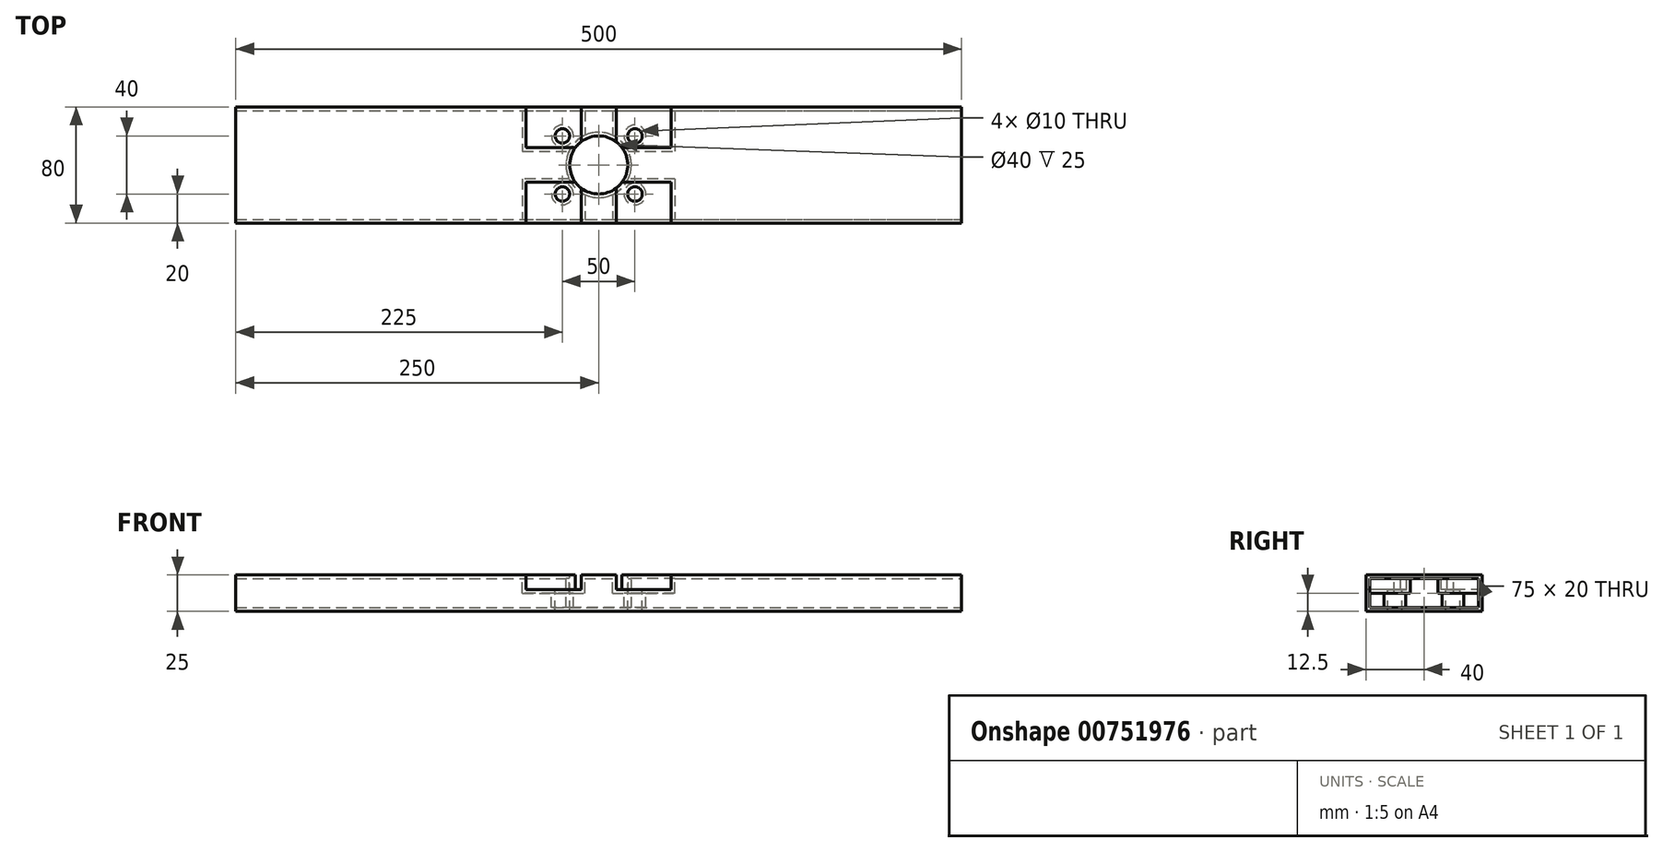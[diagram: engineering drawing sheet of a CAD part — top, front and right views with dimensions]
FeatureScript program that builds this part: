
annotation { "Feature Type Name" : "Feature", "Feature Type Description" : "" }
export const myFeature = defineFeature(function(context is Context, id is Id, definition is map)
    precondition{}
    {
        {
            var Q0;
            Q0=qCreatedBy(makeId("Top.planeOp"),FACE);
            var sketch = newSketch(context, id + "F0", { "sketchPlane" : qUnion([Q0])});
            skLineSegment(sketch, "E0.bottom", {"start": v(-250, 40) * mm, "end": v(250, 40) * mm});
            skLineSegment(sketch, "E0.top", {"start": v(-250, -40) * mm, "end": v(250, -40) * mm});
            skLineSegment(sketch, "E0.left", {"start": v(-250, 40) * mm, "end": v(-250, -40) * mm});
            skLineSegment(sketch, "E0.right", {"start": v(250, 40) * mm, "end": v(250, -40) * mm});
            skPoint(sketch, "E0.middle", {"position": v(0, 0) * mm});
            skSolve(sketch);
        }
        {
            var Q0;
            Q0=makeQuery(id+"F0.imprint","IMPRINT",FACE,{"disambiguationData":[TD([[makeQuery(id+"F0.imprint","IMPRINT",EDGE,{"derivedFrom":sQuery(id+"F0.wireOp",EDGE,"E0.bottom")}),-1.0]])]});
            extrude(context, id + "F1", {"entities" : qUnion([Q0]), "depth" : 25 * mm, "offsetDistance" : 25 * mm});
        }
        {
            var Q0;
            Q0=makeQuery(id+"F1.opExtrude","CAP_FACE",FACE,{"disambiguationData":[OSD([sQuery(id+"F0.wireOp",EDGE,"E0.bottom"),sQuery(id+"F0.wireOp",EDGE,"E0.top"),sQuery(id+"F0.wireOp",EDGE,"E0.left"),sQuery(id+"F0.wireOp",EDGE,"E0.right")])],"isStart":false});
            var sketch = newSketch(context, id + "F2", { "sketchPlane" : qUnion([Q0])});
            skLineSegment(sketch, "E1", {"start": v(0, 40) * mm, "end": v(0, -40) * mm, "construction": true});
            skLineSegment(sketch, "E2", {"start": v(-50, 40) * mm, "end": v(-50, -40) * mm});
            skLineSegment(sketch, "E3", {"start": v(50, 40) * mm, "end": v(50, -40) * mm});
            skLineSegment(sketch, "E4", {"start": v(-50, 0) * mm, "end": v(0, 0) * mm, "construction": true});
            skLineSegment(sketch, "E5", {"start": v(0, 0) * mm, "end": v(50, 0) * mm, "construction": true});
            skLineSegment(sketch, "E6", {"start": v(-25, 0) * mm, "end": v(-25, 40) * mm, "construction": true});
            skLineSegment(sketch, "E7", {"start": v(-25, 0) * mm, "end": v(-25, -40) * mm, "construction": true});
            skLineSegment(sketch, "E8", {"start": v(25, 0) * mm, "end": v(25, 40) * mm, "construction": true});
            skLineSegment(sketch, "E9", {"start": v(25, 0) * mm, "end": v(25, -40) * mm, "construction": true});
            skPoint(sketch, "E10", {"position": v(-25, 20) * mm});
            skPoint(sketch, "E11", {"position": v(25, 20) * mm});
            skPoint(sketch, "E12", {"position": v(25, -20) * mm});
            skPoint(sketch, "E13", {"position": v(-25, -20) * mm});
            skLineSegment(sketch, "E14", {"start": v(-12, 40) * mm, "end": v(-12, -40) * mm});
            skLineSegment(sketch, "E15", {"start": v(12, 40) * mm, "end": v(12, -40) * mm});
            skLineSegment(sketch, "E16", {"start": v(-50, 12) * mm, "end": v(50, 12) * mm});
            skLineSegment(sketch, "E17", {"start": v(50, -12) * mm, "end": v(-50, -12) * mm});
            skSolve(sketch);
        }
        {
            var Q0;
            Q0=sQuery(id+"F2.wireOp",VERTEX,"E5.start");
            var Q1;
            Q1=makeQuery(id+"F1.opExtrude","SWEPT_BODY",BODY,{"disambiguationData":[OSD([sQuery(id+"F0.wireOp",EDGE,"E0.bottom"),sQuery(id+"F0.wireOp",EDGE,"E0.top"),sQuery(id+"F0.wireOp",EDGE,"E0.left"),sQuery(id+"F0.wireOp",EDGE,"E0.right")])]});
            hole(context, id + "F3", {"style" : HoleStyle.SIMPLE, "endStyle" : HoleEndStyle.BLIND, "holeDiameter" : 40 * mm, "majorDiameter" : 5 * mm, "holeDepth" : 25 * mm, "isTappedThrough" : true, "tappedDepth" : 12 * mm, "tapClearance" : 3, "startFromSketch" : true, "locations" : qUnion([Q0]), "scope" : qUnion([Q1])});
        }
        {
            var Q0;
            Q0=sQuery(id+"F2.wireOp",VERTEX,"E10");
            var Q1;
            Q1=sQuery(id+"F2.wireOp",VERTEX,"E11");
            var Q2;
            Q2=sQuery(id+"F2.wireOp",VERTEX,"E12");
            var Q3;
            Q3=sQuery(id+"F2.wireOp",VERTEX,"E13");
            var Q4;
            Q4=makeQuery(id+"F1.opExtrude","SWEPT_BODY",BODY,{"disambiguationData":[OSD([sQuery(id+"F0.wireOp",EDGE,"E0.bottom"),sQuery(id+"F0.wireOp",EDGE,"E0.top"),sQuery(id+"F0.wireOp",EDGE,"E0.left"),sQuery(id+"F0.wireOp",EDGE,"E0.right")])]});
            hole(context, id + "F4", {"style" : HoleStyle.SIMPLE, "endStyle" : HoleEndStyle.BLIND, "holeDiameter" : 10 * mm, "majorDiameter" : 5 * mm, "holeDepth" : 25 * mm, "isTappedThrough" : true, "tappedDepth" : 12 * mm, "tapClearance" : 3, "startFromSketch" : true, "locations" : qUnion([Q0, Q1, Q2, Q3]), "scope" : qUnion([Q4])});
        }
        {
            var Q0;
            {var subQ0=sQuery(id+"F2.wireOp",EDGE,"E2");var subQ1=makeQuery(id+"F1.opExtrude","CAP_EDGE",EDGE,{"disambiguationData":[OSD([sQuery(id+"F0.wireOp",EDGE,"E0.top")])],"isStart":false});var subQ2=makeQuery(id+"F2.imprint","INTERSECT",VERTEX,{"derivedFrom":[subQ1,subQ0]});Q0=makeQuery(id+"F2.imprint","IMPRINT",FACE,{"disambiguationData":[TD([[makeQuery(id+"F2.imprint","IMPRINT",EDGE,{"disambiguationData":[TD([[subQ2,1.0]])],"derivedFrom":subQ0}),1.0]])]});}
            var Q1;
            {var subQ0=sQuery(id+"F2.wireOp",EDGE,"E2");var subQ1=makeQuery(id+"F1.opExtrude","CAP_EDGE",EDGE,{"disambiguationData":[OSD([sQuery(id+"F0.wireOp",EDGE,"E0.bottom")])],"isStart":false});var subQ2=makeQuery(id+"F2.imprint","INTERSECT",VERTEX,{"derivedFrom":[subQ1,subQ0]});Q1=makeQuery(id+"F2.imprint","IMPRINT",FACE,{"disambiguationData":[TD([[makeQuery(id+"F2.imprint","IMPRINT",EDGE,{"disambiguationData":[TD([[subQ2,-1.0]])],"derivedFrom":subQ0}),1.0]])]});}
            var Q2;
            {var subQ0=sQuery(id+"F2.wireOp",EDGE,"E3");var subQ1=makeQuery(id+"F1.opExtrude","CAP_EDGE",EDGE,{"disambiguationData":[OSD([sQuery(id+"F0.wireOp",EDGE,"E0.bottom")])],"isStart":false});var subQ2=makeQuery(id+"F2.imprint","INTERSECT",VERTEX,{"derivedFrom":[subQ1,subQ0]});Q2=makeQuery(id+"F2.imprint","IMPRINT",FACE,{"disambiguationData":[TD([[makeQuery(id+"F2.imprint","IMPRINT",EDGE,{"disambiguationData":[TD([[subQ2,-1.0]])],"derivedFrom":subQ0}),-1.0]])]});}
            var Q3;
            {var subQ0=sQuery(id+"F2.wireOp",EDGE,"E3");var subQ1=makeQuery(id+"F1.opExtrude","CAP_EDGE",EDGE,{"disambiguationData":[OSD([sQuery(id+"F0.wireOp",EDGE,"E0.top")])],"isStart":false});var subQ2=makeQuery(id+"F2.imprint","INTERSECT",VERTEX,{"derivedFrom":[subQ1,subQ0]});Q3=makeQuery(id+"F2.imprint","IMPRINT",FACE,{"disambiguationData":[TD([[makeQuery(id+"F2.imprint","IMPRINT",EDGE,{"disambiguationData":[TD([[subQ2,1.0]])],"derivedFrom":subQ0}),-1.0]])]});}
            extrude(context, id + "F5", {"entities" : qUnion([Q0, Q1, Q2, Q3]), "operationType" : NewBodyOperationType.REMOVE, "oppositeDirection" : true, "depth" : 10 * mm, "offsetDistance" : 25 * mm});
        }
        {
            var Q0;
            Q0=makeQuery(id+"F1.opExtrude","SWEPT_FACE",FACE,{"disambiguationData":[OSD([sQuery(id+"F0.wireOp",EDGE,"E0.left")])]});
            var Q1;
            Q1=makeQuery(id+"F1.opExtrude","SWEPT_FACE",FACE,{"disambiguationData":[OSD([sQuery(id+"F0.wireOp",EDGE,"E0.right")])]});
            var Q2;
            Q2=makeQuery(id+"F1.opExtrude","SWEPT_BODY",BODY,{"disambiguationData":[OSD([sQuery(id+"F0.wireOp",EDGE,"E0.bottom"),sQuery(id+"F0.wireOp",EDGE,"E0.top"),sQuery(id+"F0.wireOp",EDGE,"E0.left"),sQuery(id+"F0.wireOp",EDGE,"E0.right")])]});
            shell(context, id + "F6", {"entities" : qUnion([Q0, Q1]), "parts" : qUnion([Q2]), "thickness" : 2.5 * mm});
        }
    });
